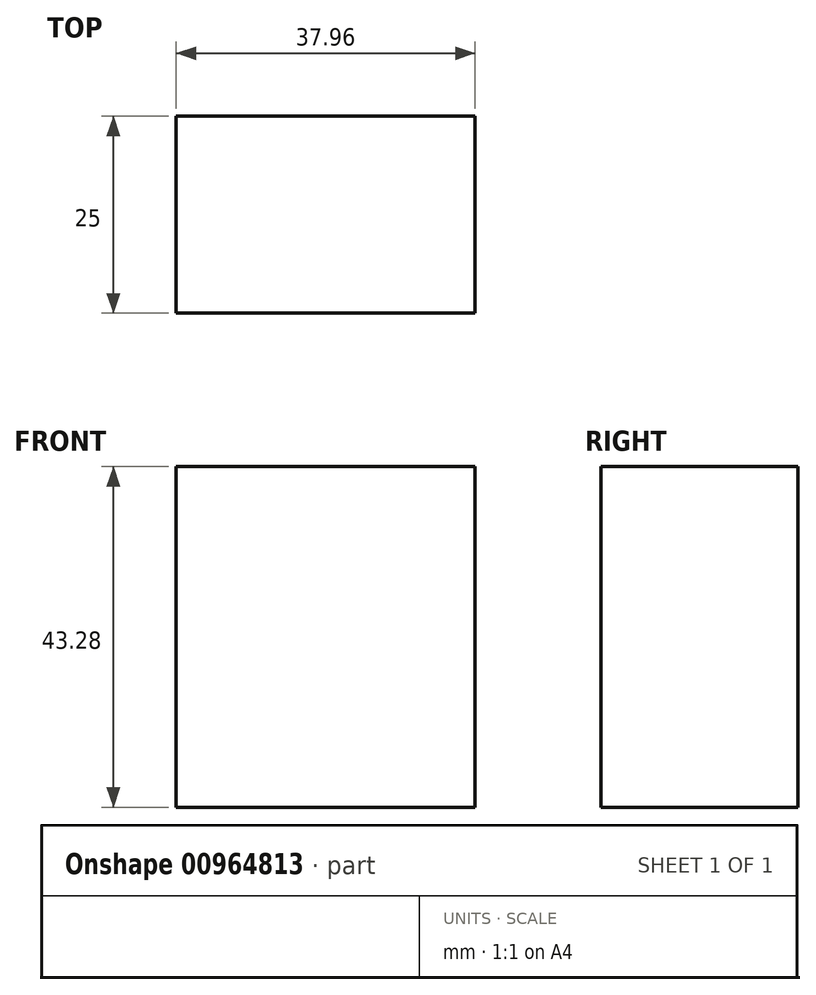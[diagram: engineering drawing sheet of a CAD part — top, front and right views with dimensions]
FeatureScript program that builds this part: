
annotation { "Feature Type Name" : "Feature", "Feature Type Description" : "" }
export const myFeature = defineFeature(function(context is Context, id is Id, definition is map)
    precondition{}
    {
        {
            var Q0;
            Q0=qCreatedBy(makeId("Front.planeOp"),FACE);
            var sketch = newSketch(context, id + "F0", { "sketchPlane" : qUnion([Q0])});
            skLineSegment(sketch, "E0.bottom", {"start": v(-135.78, 57.83) * mm, "end": v(-97.82, 57.83) * mm});
            skLineSegment(sketch, "E0.top", {"start": v(-135.78, 14.55) * mm, "end": v(-97.82, 14.55) * mm});
            skLineSegment(sketch, "E0.left", {"start": v(-135.78, 57.83) * mm, "end": v(-135.78, 14.55) * mm});
            skLineSegment(sketch, "E0.right", {"start": v(-97.82, 57.83) * mm, "end": v(-97.82, 14.55) * mm});
            skSolve(sketch);
        }
        {
            var Q0;
            Q0 = qSketchRegion(id + "F0", true);
            extrude(context, id + "F1", {"entities" : qUnion([Q0]), "depth" : 25 * mm, "offsetDistance" : 25 * mm});
        }
    });
